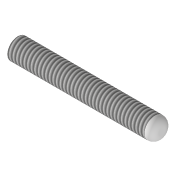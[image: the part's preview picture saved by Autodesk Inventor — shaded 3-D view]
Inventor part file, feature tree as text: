
AUTODESK INVENTOR PART (.ipt)
format: ipt  version: 2022 (Build 260153000, 153)  size: 94,208 bytes
history: native  units: mm
features: extrude x1, fillet x1, thread x1, sketch x1
ambient origin geometry x8: Origin, YZ Plane, XZ Plane, XY Plane, X Axis, Y Axis, Z Axis, Center Point
bodies: Volumenkörper1 (feature_tree)
feature tree (4):
  extrude  "Extrusion1"  Depth=20.0mm TaperAngle=0.0deg
  fillet  "Rundung1"  Radius=1.0mm
  thread  "Gewinde1"  [1 undecoded]
  sketch  "Skizze1"  dims[d0=2.9mm d1=20.0mm d2=0.0mm d3=1.0mm d4=19.0mm d5=0.0mm]
note: 1 required parameter value undecoded (feature->parameter linkage not recoverable at this tier; creation-order binding heuristic only, values carry confidence <= 0.55)
